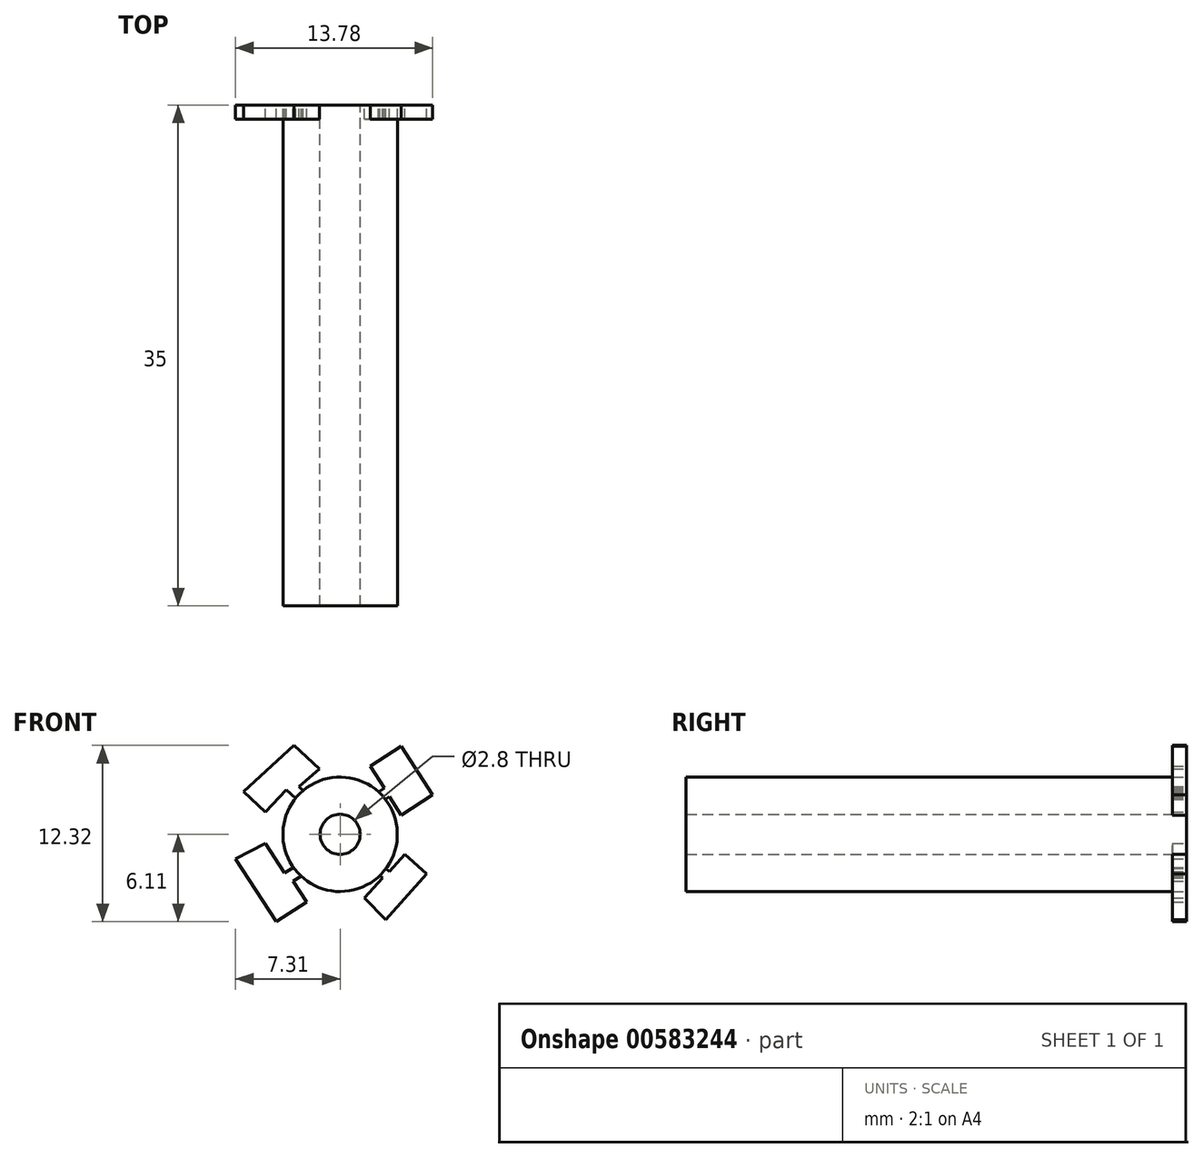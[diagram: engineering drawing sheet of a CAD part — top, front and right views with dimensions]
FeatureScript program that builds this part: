
annotation { "Feature Type Name" : "Feature", "Feature Type Description" : "" }
export const myFeature = defineFeature(function(context is Context, id is Id, definition is map)
    precondition{}
    {
        {
            var Q0;
            Q0=qCreatedBy(makeId("Front.planeOp"),FACE);
            var sketch = newSketch(context, id + "F0", { "sketchPlane" : qUnion([Q0])});
            skCircle(sketch, "E0", {"center": v(0, 0) * mm, "radius": 1.4 * mm});
            skCircle(sketch, "E1", {"center": v(0, 0) * mm, "radius": 4 * mm});
            skSolve(sketch);
        }
        {
            var Q0;
            Q0=makeQuery(id+"F0.imprint","IMPRINT",FACE,{"disambiguationData":[TD([[makeQuery(id+"F0.imprint","IMPRINT",EDGE,{"derivedFrom":sQuery(id+"F0.wireOp",EDGE,"E0")}),-1.0]])]});
            extrude(context, id + "F1", {"entities" : qUnion([Q0]), "depth" : 35 * mm, "offsetDistance" : 25 * mm});
        }
        {
            var Q0;
            Q0=makeQuery(id+"F1.opExtrude","CAP_FACE",FACE,{"disambiguationData":[OSD([sQuery(id+"F0.wireOp",EDGE,"E0"),sQuery(id+"F0.wireOp",EDGE,"E1")])],"isStart":true});
            var sketch = newSketch(context, id + "F2", { "sketchPlane" : qUnion([Q0])});
            skSolve(sketch);
        }
        {
            var Q0;
            Q0=makeQuery(id+"F2.imprint","IMPRINT",FACE,{"disambiguationData":[TD([[makeQuery(id+"F2.imprint","IMPRINT",EDGE,{"derivedFrom":makeQuery(id+"F1.opExtrude","CAP_EDGE",EDGE,{"disambiguationData":[OSD([sQuery(id+"F0.wireOp",EDGE,"E0")])],"isStart":true})}),1.0]])]});
            var sketch = newSketch(context, id + "F3", { "sketchPlane" : qUnion([Q0])});
            skLineSegment(sketch, "E2", {"start": v(-2.66, 2.12) * mm, "end": v(-3.44, 2.62) * mm});
            skLineSegment(sketch, "E3", {"start": v(-3.44, 2.62) * mm, "end": v(-4.27, 1.33) * mm});
            skLineSegment(sketch, "E4", {"start": v(-4.27, 1.33) * mm, "end": v(-6.47, 2.75) * mm});
            skLineSegment(sketch, "E5", {"start": v(-6.47, 2.75) * mm, "end": v(-4.27, 6.15) * mm});
            skLineSegment(sketch, "E6", {"start": v(-4.27, 6.15) * mm, "end": v(-2.12, 4.77) * mm});
            skLineSegment(sketch, "E7", {"start": v(-2.12, 4.77) * mm, "end": v(-3.1, 3.23) * mm});
            skLineSegment(sketch, "E8", {"start": v(-3.1, 3.23) * mm, "end": v(-2.16, 2.62) * mm});
            skLineSegment(sketch, "E9", {"start": v(-2.16, 2.62) * mm, "end": v(-2.53, 2.05) * mm});
            skLineSegment(sketch, "E10", {"start": v(-2.53, 2.05) * mm, "end": v(-2.66, 2.12) * mm});
            skLineSegment(sketch, "E11", {"start": v(2.14, 2.62) * mm, "end": v(2.86, 3.32) * mm});
            skLineSegment(sketch, "E12", {"start": v(2.86, 3.32) * mm, "end": v(1.45, 4.57) * mm});
            skLineSegment(sketch, "E13", {"start": v(1.45, 4.57) * mm, "end": v(3.22, 6.2) * mm});
            skLineSegment(sketch, "E14", {"start": v(3.22, 6.2) * mm, "end": v(6.74, 2.98) * mm});
            skLineSegment(sketch, "E15", {"start": v(6.74, 2.98) * mm, "end": v(5.24, 1.55) * mm});
            skLineSegment(sketch, "E16", {"start": v(5.24, 1.55) * mm, "end": v(3.76, 3.1) * mm});
            skLineSegment(sketch, "E17", {"start": v(3.76, 3.1) * mm, "end": v(2.65, 2.12) * mm});
            skLineSegment(sketch, "E18", {"start": v(2.65, 2.12) * mm, "end": v(2.14, 2.62) * mm});
            skLineSegment(sketch, "E19", {"start": v(-2.66, -1.91) * mm, "end": v(-3.44, -2.61) * mm});
            skLineSegment(sketch, "E20", {"start": v(-3.44, -2.61) * mm, "end": v(-4.52, -1.4) * mm});
            skLineSegment(sketch, "E21", {"start": v(-4.52, -1.4) * mm, "end": v(-6.04, -2.76) * mm});
            skLineSegment(sketch, "E22", {"start": v(-6.04, -2.76) * mm, "end": v(-3.18, -5.96) * mm});
            skLineSegment(sketch, "E23", {"start": v(-3.18, -5.96) * mm, "end": v(-1.7, -4.46) * mm});
            skLineSegment(sketch, "E24", {"start": v(-1.7, -4.46) * mm, "end": v(-2.96, -3.05) * mm});
            skLineSegment(sketch, "E25", {"start": v(-2.96, -3.05) * mm, "end": v(-2.26, -2.42) * mm});
            skLineSegment(sketch, "E26", {"start": v(-2.26, -2.42) * mm, "end": v(-2.66, -1.91) * mm});
            skLineSegment(sketch, "E27", {"start": v(2.65, -1.91) * mm, "end": v(3.88, -2.7) * mm});
            skLineSegment(sketch, "E28", {"start": v(3.88, -2.7) * mm, "end": v(5.21, -0.63) * mm});
            skLineSegment(sketch, "E29", {"start": v(5.21, -0.63) * mm, "end": v(7.31, -1.7) * mm});
            skLineSegment(sketch, "E30", {"start": v(7.31, -1.7) * mm, "end": v(4.47, -6.1) * mm});
            skLineSegment(sketch, "E31", {"start": v(4.47, -6.1) * mm, "end": v(2.34, -4.74) * mm});
            skLineSegment(sketch, "E32", {"start": v(2.34, -4.74) * mm, "end": v(3.28, -3.29) * mm});
            skLineSegment(sketch, "E33", {"start": v(3.28, -3.29) * mm, "end": v(2.14, -2.55) * mm});
            skLineSegment(sketch, "E34", {"start": v(2.14, -2.55) * mm, "end": v(2.65, -1.91) * mm});
            skSolve(sketch);
        }
        {
            var Q0;
            {var subQ0=sQuery(id+"F3.wireOp",EDGE,"E3");Q0=makeQuery(id+"F3.imprint","IMPRINT",FACE,{"disambiguationData":[TD([[makeQuery(id+"F3.imprint","IMPRINT",EDGE,{"derivedFrom":subQ0}),-1.0]])]});}
            var Q1;
            {var subQ0=sQuery(id+"F3.wireOp",EDGE,"E20");Q1=makeQuery(id+"F3.imprint","IMPRINT",FACE,{"disambiguationData":[TD([[makeQuery(id+"F3.imprint","IMPRINT",EDGE,{"derivedFrom":subQ0}),1.0]])]});}
            var Q2;
            {var subQ0=sQuery(id+"F3.wireOp",EDGE,"E28");Q2=makeQuery(id+"F3.imprint","IMPRINT",FACE,{"disambiguationData":[TD([[makeQuery(id+"F3.imprint","IMPRINT",EDGE,{"derivedFrom":subQ0}),-1.0]])]});}
            var Q3;
            {var subQ5=sQuery(id+"F3.wireOp",EDGE,"E12");Q3=makeQuery(id+"F3.imprint","IMPRINT",FACE,{"disambiguationData":[TD([[makeQuery(id+"F3.imprint","IMPRINT",EDGE,{"derivedFrom":subQ5}),-1.0]])]});}
            extrude(context, id + "F4", {"entities" : qUnion([Q0, Q1, Q2, Q3]), "operationType" : NewBodyOperationType.ADD, "oppositeDirection" : true, "depth" : 1 * mm, "offsetDistance" : 25 * mm});
        }
    });
